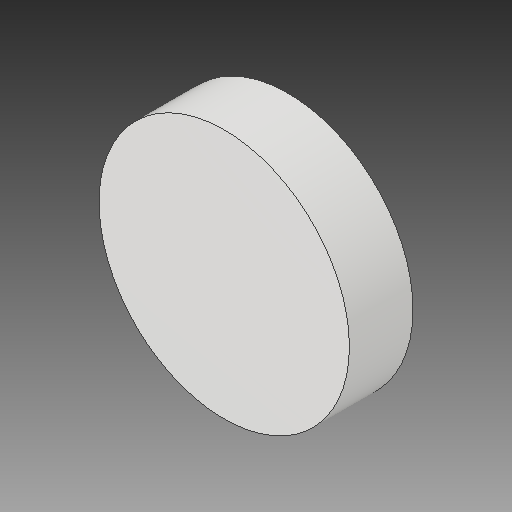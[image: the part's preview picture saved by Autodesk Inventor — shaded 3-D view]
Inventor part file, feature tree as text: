
AUTODESK INVENTOR PART (.ipt)
format: ipt  version: 2019 (Build 230136000, 136)  size: 97,280 bytes
history: native  units: in
note: dims shown in document units (in); Inventor stores cm internally (conversion verified against a paired STEP export)
features: other x4, reference x2, extrude x1, sketch x1
ambient origin geometry x8: Origin, YZ Plane, XZ Plane, XY Plane, X Axis, Y Axis, Z Axis, Center Point
bodies: Solid1 (feature_tree)
feature tree (8):
  extrude  "Extrusion1"  Depth=0.6in
  sketch  "Sketch1"  dims[d0=2.5in d1=12.0in d2=2.3622in d3=0.6in d4=0.0in]
  reference  "Reference1"
  reference  "Reference2"
  other  "<userpath>\Desktop\Roombotics\UpperLevel.iam"
  other  "UpperLevel.iam"
  other  "Top:1"
  other  "Stove:1"
